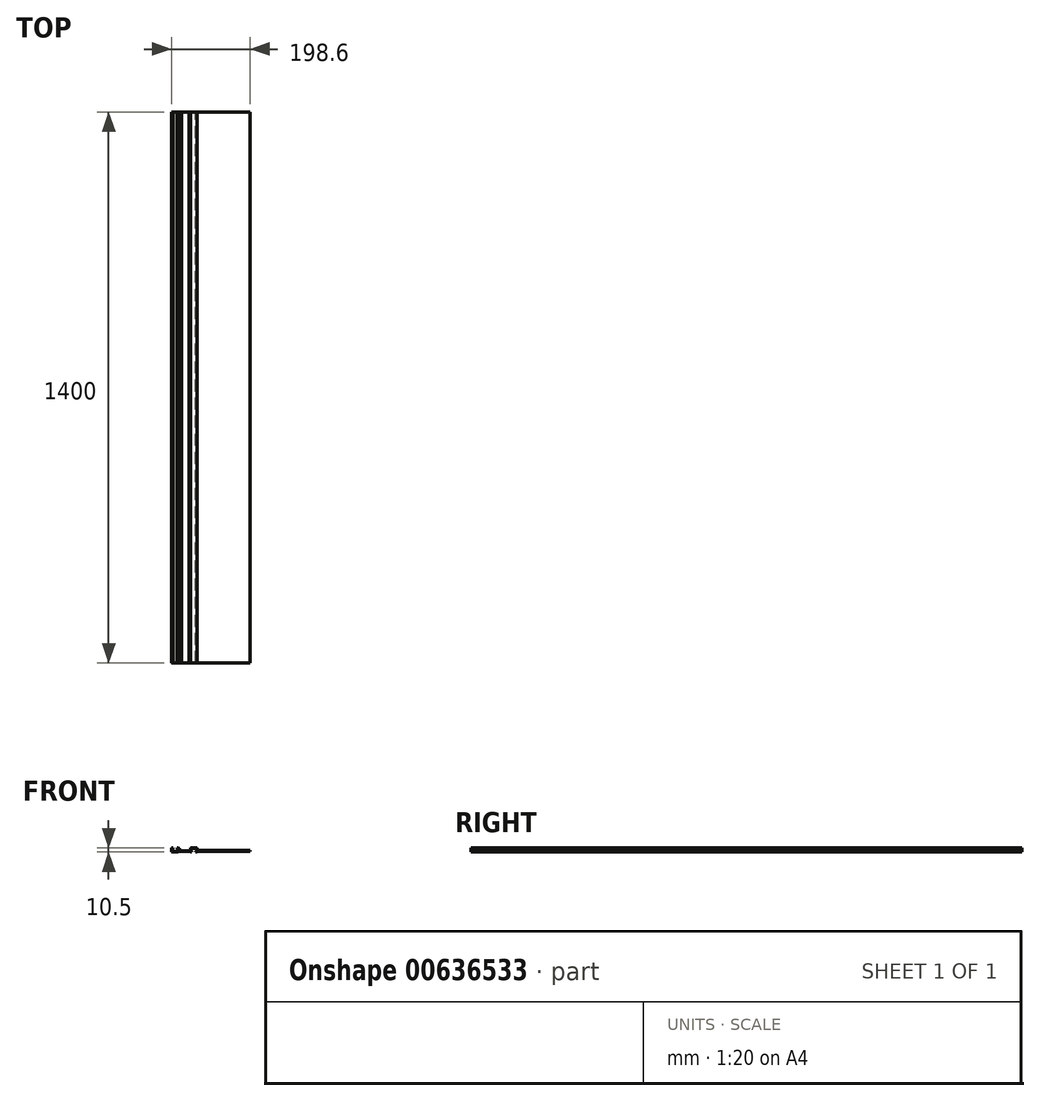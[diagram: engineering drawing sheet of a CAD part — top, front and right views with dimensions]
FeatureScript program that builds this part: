
annotation { "Feature Type Name" : "Feature", "Feature Type Description" : "" }
export const myFeature = defineFeature(function(context is Context, id is Id, definition is map)
    precondition{}
    {
        {
            var Q0;
            Q0=qCreatedBy(makeId("Front.planeOp"),FACE);
            var sketch = newSketch(context, id + "F0", { "sketchPlane" : qUnion([Q0])});
            skLineSegment(sketch, "E0.bottom", {"start": v(0, 0) * mm, "end": v(-15, 0) * mm});
            skLineSegment(sketch, "E0.top", {"start": v(-1, 10.5) * mm, "end": v(-3, 10.5) * mm});
            skLineSegment(sketch, "E0.left", {"start": v(0, 0) * mm, "end": v(0, 1.5) * mm});
            skLineSegment(sketch, "E0.right", {"start": v(-16, 1) * mm, "end": v(-16, 9.5) * mm});
            skLineSegment(sketch, "E1.0", {"start": v(-14.5, 1.5) * mm, "end": v(-14.5, 9) * mm});
            skLineSegment(sketch, "E1.1", {"start": v(-1.5, 1.5) * mm, "end": v(-14.5, 1.5) * mm});
            skLineSegment(sketch, "E1.2", {"start": v(-1.5, 1.5) * mm, "end": v(-1.5, 9) * mm});
            skLineSegment(sketch, "E1.3", {"start": v(-1.5, 9) * mm, "end": v(-3, 9) * mm});
            skPoint(sketch, "E2.visualSharp", {"position": v(-16, 10.5) * mm});
            skArc(sketch, "E2.filletArc", {"start": v(-15, 10.5) * mm, "mid": v(-15.7, 10.2) * mm, "end": v(-16, 9.5) * mm});
            skPoint(sketch, "E3.visualSharp", {"position": v(0, 10.5) * mm});
            skArc(sketch, "E3.filletArc", {"start": v(0, 9.5) * mm, "mid": v(-0.3, 10.2) * mm, "end": v(-1, 10.5) * mm});
            skPoint(sketch, "E4.visualSharp", {"position": v(-16, 0) * mm});
            skArc(sketch, "E4.filletArc", {"start": v(-16, 1) * mm, "mid": v(-15.7, 0.3) * mm, "end": v(-15, 0) * mm});
            skLineSegment(sketch, "E5", {"start": v(-8, 1.5) * mm, "end": v(-8, 5.16) * mm, "construction": true});
            skLineSegment(sketch, "E6", {"start": v(-13, 10.5) * mm, "end": v(-13, 9) * mm});
            skLineSegment(sketch, "E7.MirrorCS", {"start": v(-3, 10.5) * mm, "end": v(-3, 9) * mm});
            skLineSegment(sketch, "E8.trimOffspring", {"start": v(-13, 10.5) * mm, "end": v(-15, 10.5) * mm});
            skLineSegment(sketch, "E9.trimOffspring", {"start": v(-13, 9) * mm, "end": v(-14.5, 9) * mm});
            skLineSegment(sketch, "E10.bottom", {"start": v(0, 4) * mm, "end": v(8, 4) * mm});
            skLineSegment(sketch, "E10.top", {"start": v(0, 1.5) * mm, "end": v(32, 1.5) * mm});
            skLineSegment(sketch, "E11.bottom", {"start": v(32, 0) * mm, "end": v(35, 0) * mm});
            skLineSegment(sketch, "E11.top", {"start": v(33, 10.5) * mm, "end": v(47, 10.5) * mm});
            skLineSegment(sketch, "E11.left", {"start": v(32, 0) * mm, "end": v(32, 1.5) * mm});
            skLineSegment(sketch, "E11.right", {"start": v(48, 0) * mm, "end": v(48, 1.5) * mm});
            skLineSegment(sketch, "E12.0", {"start": v(33.5, 1.5) * mm, "end": v(33.5, 9) * mm});
            skLineSegment(sketch, "E12.1", {"start": v(33.5, 1.5) * mm, "end": v(35, 1.5) * mm});
            skLineSegment(sketch, "E12.2", {"start": v(46.5, 1.5) * mm, "end": v(46.5, 9) * mm});
            skLineSegment(sketch, "E12.3", {"start": v(33.5, 9) * mm, "end": v(46.5, 9) * mm});
            skPoint(sketch, "E13.visualSharp", {"position": v(32, 10.5) * mm});
            skArc(sketch, "E13.filletArc", {"start": v(33, 10.5) * mm, "mid": v(32.3, 10.2) * mm, "end": v(32, 9.5) * mm});
            skPoint(sketch, "E14.visualSharp", {"position": v(48, 10.5) * mm});
            skArc(sketch, "E14.filletArc", {"start": v(48, 9.5) * mm, "mid": v(47.7, 10.2) * mm, "end": v(47, 10.5) * mm});
            skLineSegment(sketch, "E15", {"start": v(40, 1.5) * mm, "end": v(40, 3.5) * mm, "construction": true});
            skLineSegment(sketch, "E16", {"start": v(35, 1.5) * mm, "end": v(35, 0) * mm});
            skLineSegment(sketch, "E17.MirrorCS", {"start": v(45, 1.5) * mm, "end": v(45, 0) * mm});
            skLineSegment(sketch, "E18.trimOffspring", {"start": v(45, 0) * mm, "end": v(48, 0) * mm});
            skLineSegment(sketch, "E19.trimOffspring", {"start": v(45, 1.5) * mm, "end": v(46.5, 1.5) * mm});
            skLineSegment(sketch, "E20.bottom", {"start": v(48, 4) * mm, "end": v(182.6, 4) * mm});
            skLineSegment(sketch, "E20.top", {"start": v(48, 1.5) * mm, "end": v(182.6, 1.5) * mm});
            skLineSegment(sketch, "E20.right", {"start": v(182.6, 4) * mm, "end": v(182.6, 1.5) * mm});
            skLineSegment(sketch, "E21.trimOffspring", {"start": v(0, 4) * mm, "end": v(0, 7) * mm});
            skLineSegment(sketch, "E22.trimOffspring", {"start": v(32, 4) * mm, "end": v(32, 9.5) * mm});
            skLineSegment(sketch, "E23.trimOffspring", {"start": v(48, 4) * mm, "end": v(48, 9.5) * mm});
            skLineSegment(sketch, "E24.bottom", {"start": v(0, 9.5) * mm, "end": v(3, 9.5) * mm});
            skLineSegment(sketch, "E24.top", {"start": v(0, 7) * mm, "end": v(3, 7) * mm});
            skLineSegment(sketch, "E24.right", {"start": v(4, 8.5) * mm, "end": v(4, 8) * mm});
            skPoint(sketch, "E25.visualSharp", {"position": v(4, 9.5) * mm});
            skArc(sketch, "E25.filletArc", {"start": v(4, 8.5) * mm, "mid": v(3.7, 9.2) * mm, "end": v(3, 9.5) * mm});
            skPoint(sketch, "E26.visualSharp", {"position": v(4, 7) * mm});
            skArc(sketch, "E26.filletArc", {"start": v(3, 7) * mm, "mid": v(3.7, 7.3) * mm, "end": v(4, 8) * mm});
            skLineSegment(sketch, "E27", {"start": v(29, 4) * mm, "end": v(28.57, 3.25) * mm});
            skLineSegment(sketch, "E28", {"start": v(28.57, 3.25) * mm, "end": v(8.43, 3.25) * mm});
            skLineSegment(sketch, "E29", {"start": v(8.43, 3.25) * mm, "end": v(8, 4) * mm});
            skLineSegment(sketch, "E30.trimOffspring", {"start": v(29, 4) * mm, "end": v(32, 4) * mm});
            skSolve(sketch);
        }
        {
            var Q0;
            Q0=makeQuery(id+"F0.imprint","IMPRINT",FACE,{"disambiguationData":[TD([[makeQuery(id+"F0.imprint","IMPRINT",EDGE,{"derivedFrom":sQuery(id+"F0.wireOp",EDGE,"E0.bottom")}),-1.0]])]});
            extrude(context, id + "F1", {"entities" : qUnion([Q0]), "depth" : 1400 * mm, "offsetDistance" : 25 * mm});
        }
    });
